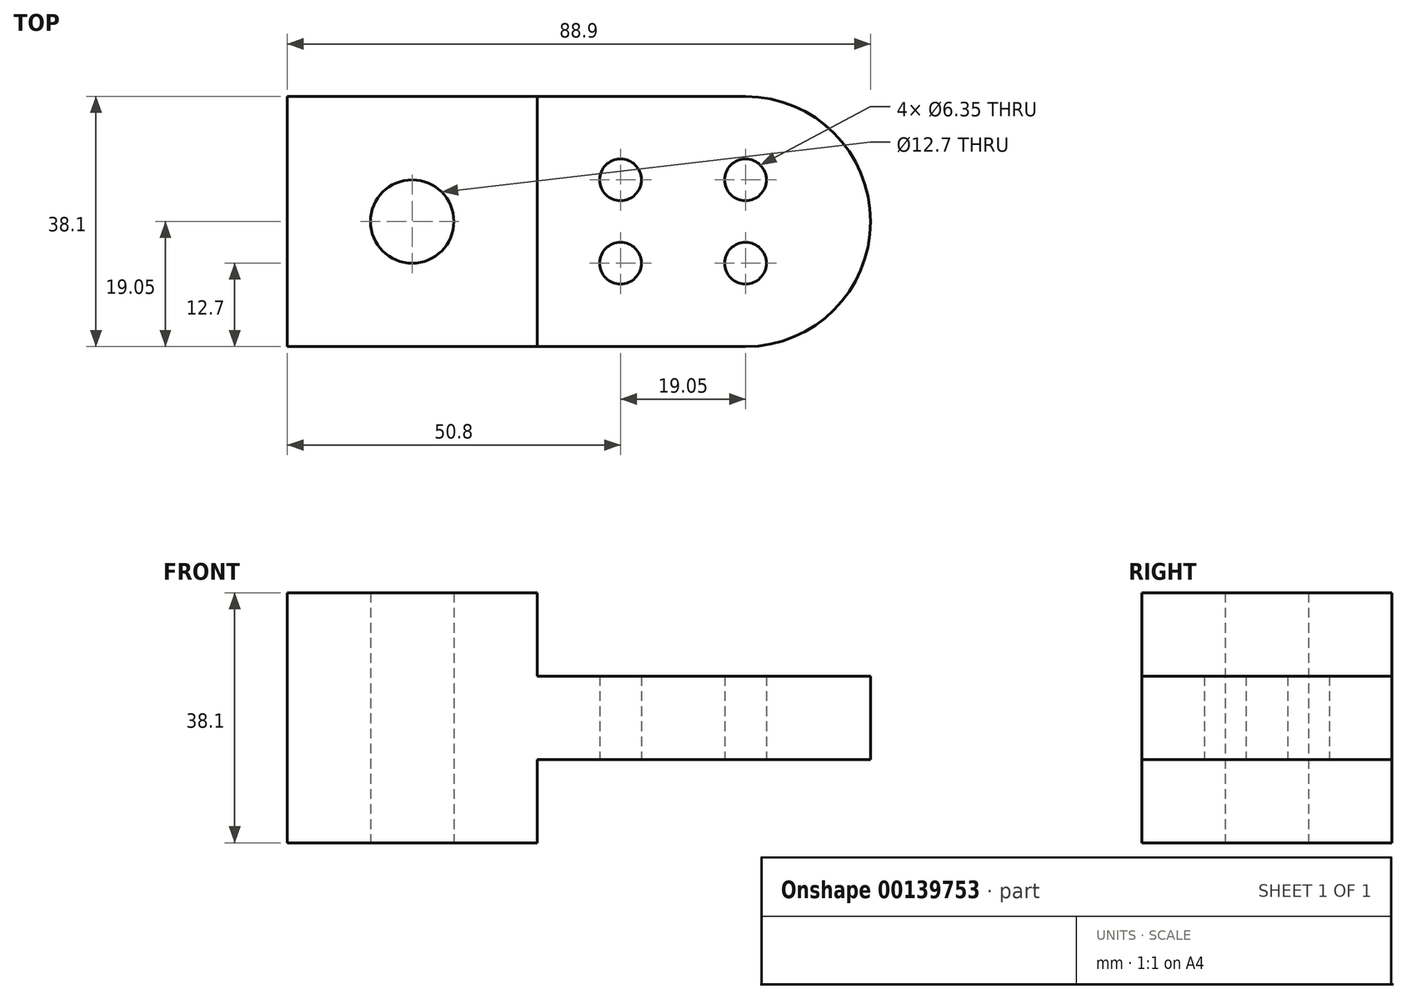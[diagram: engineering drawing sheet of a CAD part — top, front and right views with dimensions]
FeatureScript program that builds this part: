
annotation { "Feature Type Name" : "Feature", "Feature Type Description" : "" }
export const myFeature = defineFeature(function(context is Context, id is Id, definition is map)
    precondition{}
    {
        {
            var Q0;
            Q0=qCreatedBy(makeId("Top.planeOp"),FACE);
            var sketch = newSketch(context, id + "F0", { "sketchPlane" : qUnion([Q0])});
            skLineSegment(sketch, "E0.bottom", {"start": v(0, 38.1) * mm, "end": v(38.1, 38.1) * mm});
            skLineSegment(sketch, "E0.top", {"start": v(0, 0) * mm, "end": v(38.1, 0) * mm});
            skLineSegment(sketch, "E0.left", {"start": v(0, 38.1) * mm, "end": v(0, 0) * mm});
            skLineSegment(sketch, "E0.right", {"start": v(38.1, 38.1) * mm, "end": v(38.1, 0) * mm});
            skCircle(sketch, "E1", {"center": v(19.05, 19.05) * mm, "radius": 6.35 * mm});
            skLineSegment(sketch, "E2", {"start": v(38.1, 38.1) * mm, "end": v(69.85, 38.1) * mm});
            skLineSegment(sketch, "E3", {"start": v(38.1, 0) * mm, "end": v(69.85, 0) * mm});
            skArc(sketch, "E4", {"start": v(69.85, 0) * mm, "mid": v(88.9, 19.05) * mm, "end": v(69.85, 38.1) * mm});
            skCircle(sketch, "E5", {"center": v(50.8, 25.4) * mm, "radius": 3.18 * mm});
            skCircle(sketch, "E6", {"center": v(50.8, 12.7) * mm, "radius": 3.18 * mm});
            skCircle(sketch, "E7", {"center": v(69.85, 12.7) * mm, "radius": 3.18 * mm});
            skCircle(sketch, "E8", {"center": v(69.85, 25.4) * mm, "radius": 3.18 * mm});
            skSolve(sketch);
        }
        {
            var Q0;
            Q0=makeQuery(id+"F0.imprint","IMPRINT",FACE,{"disambiguationData":[TD([[makeQuery(id+"F0.imprint","IMPRINT",EDGE,{"derivedFrom":sQuery(id+"F0.wireOp",EDGE,"E0.bottom")}),-1.0]])]});
            extrude(context, id + "F1", {"entities" : qUnion([Q0]), "endBound" : BoundingType.SYMMETRIC, "depth" : 38.1 * mm});
        }
        {
            var Q0;
            Q0=makeQuery(id+"F0.imprint","IMPRINT",FACE,{"disambiguationData":[TD([[makeQuery(id+"F0.imprint","IMPRINT",EDGE,{"derivedFrom":sQuery(id+"F0.wireOp",EDGE,"E0.right")}),1.0]])]});
            extrude(context, id + "F2", {"entities" : qUnion([Q0]), "operationType" : NewBodyOperationType.ADD, "endBound" : BoundingType.SYMMETRIC, "depth" : 12.7 * mm});
        }
    });
